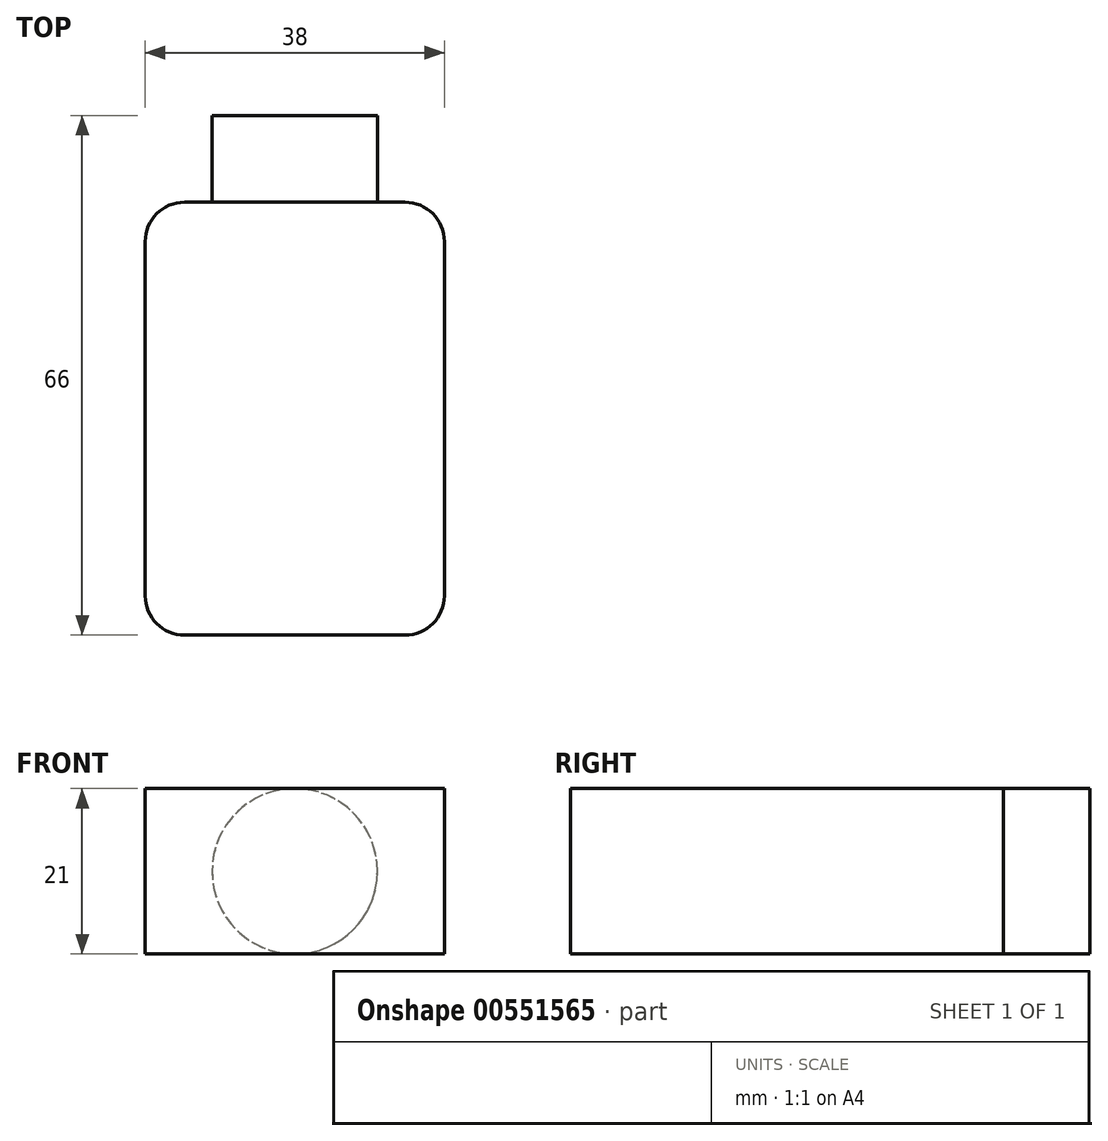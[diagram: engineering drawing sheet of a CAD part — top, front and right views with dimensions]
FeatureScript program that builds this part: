
annotation { "Feature Type Name" : "Feature", "Feature Type Description" : "" }
export const myFeature = defineFeature(function(context is Context, id is Id, definition is map)
    precondition{}
    {
        {
            var Q0;
            Q0=qCreatedBy(makeId("Top.planeOp"),FACE);
            var sketch = newSketch(context, id + "F0", { "sketchPlane" : qUnion([Q0])});
            skLineSegment(sketch, "E0.bottom", {"start": v(-7.91, 29.54) * mm, "end": v(30.09, 29.54) * mm});
            skLineSegment(sketch, "E0.top", {"start": v(-7.91, -25.46) * mm, "end": v(30.09, -25.46) * mm});
            skLineSegment(sketch, "E0.left", {"start": v(-7.91, 29.54) * mm, "end": v(-7.91, -25.46) * mm});
            skLineSegment(sketch, "E0.right", {"start": v(30.09, 29.54) * mm, "end": v(30.09, -25.46) * mm});
            skSolve(sketch);
        }
        {
            var Q0;
            Q0=makeQuery(id+"F0.imprint","IMPRINT",FACE,{"disambiguationData":[TD([[makeQuery(id+"F0.imprint","IMPRINT",EDGE,{"derivedFrom":sQuery(id+"F0.wireOp",EDGE,"E0.bottom")}),-1.0]])]});
            extrude(context, id + "F1", {"entities" : qUnion([Q0]), "depth" : 21 * mm, "offsetDistance" : 25 * mm});
        }
        {
            var Q0;
            Q0=makeQuery(id+"F1.opExtrude","SWEPT_FACE",FACE,{"disambiguationData":[OSD([sQuery(id+"F0.wireOp",EDGE,"E0.bottom")])]});
            var sketch = newSketch(context, id + "F2", { "sketchPlane" : qUnion([Q0])});
            skCircle(sketch, "E1", {"center": v(-11.09, 10.5) * mm, "radius": 10.5 * mm});
            skPoint(sketch, "E1.centerSnap0", {"position": v(-11.09, 21) * mm});
            skPoint(sketch, "E1.centerSnap1", {"position": v(-30.09, 10.5) * mm});
            skSolve(sketch);
        }
        {
            var Q0;
            {var subQ0=sQuery(id+"F2.wireOp",EDGE,"E1");var subQ1=sQuery(id+"F0.wireOp",EDGE,"E0.bottom");var subQ2=makeQuery(id+"F2.imprint","INTERSECT",VERTEX,{"derivedFrom":[makeQuery(id+"F1.opExtrude","CAP_EDGE",EDGE,{"disambiguationData":[OSD([subQ1])],"isStart":true}),subQ0]});Q0=makeQuery(id+"F2.imprint","IMPRINT",FACE,{"disambiguationData":[TD([[makeQuery(id+"F2.imprint","IMPRINT",EDGE,{"disambiguationData":[TD([[subQ2,1.0]])],"derivedFrom":subQ0}),1.0]])]});}
            extrude(context, id + "F3", {"entities" : qUnion([Q0]), "operationType" : NewBodyOperationType.ADD, "depth" : 11 * mm, "offsetDistance" : 25 * mm});
        }
        {
            var Q0;
            Q0=makeQuery(id+"F1.opExtrude","SWEPT_EDGE",EDGE,{"disambiguationData":[OSD([sQuery(id+"F0.wireOp",EDGE,"E0.bottom"),sQuery(id+"F0.wireOp",EDGE,"E0.left")])]});
            var Q1;
            Q1=makeQuery(id+"F1.opExtrude","SWEPT_EDGE",EDGE,{"disambiguationData":[OSD([sQuery(id+"F0.wireOp",EDGE,"E0.bottom"),sQuery(id+"F0.wireOp",EDGE,"E0.right")])]});
            var Q2;
            Q2=makeQuery(id+"F1.opExtrude","SWEPT_EDGE",EDGE,{"disambiguationData":[OSD([sQuery(id+"F0.wireOp",EDGE,"E0.top"),sQuery(id+"F0.wireOp",EDGE,"E0.right")])]});
            var Q3;
            Q3=makeQuery(id+"F1.opExtrude","SWEPT_EDGE",EDGE,{"disambiguationData":[OSD([sQuery(id+"F0.wireOp",EDGE,"E0.top"),sQuery(id+"F0.wireOp",EDGE,"E0.left")])]});
            fillet(context, id + "F4", {"entities" : qUnion([Q0, Q1, Q2, Q3]), "radius" : 5 * mm, "tangentPropagation" : true, "allowEdgeOverflow" : false});
        }
    });
